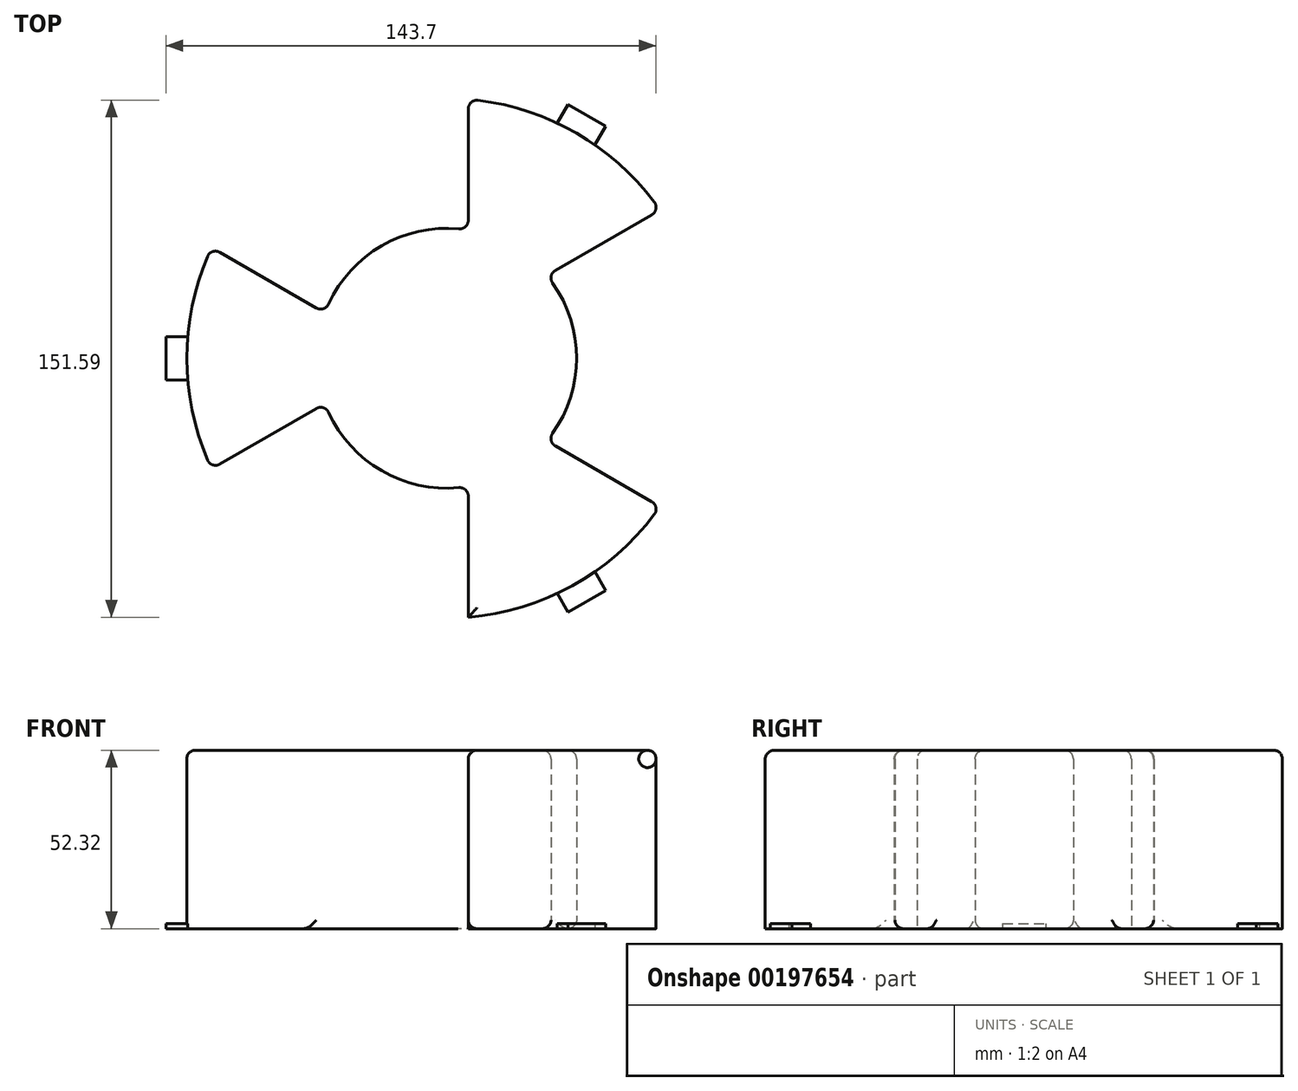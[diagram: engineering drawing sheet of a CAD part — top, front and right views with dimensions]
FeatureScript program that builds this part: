
annotation { "Feature Type Name" : "Feature", "Feature Type Description" : "" }
export const myFeature = defineFeature(function(context is Context, id is Id, definition is map)
    precondition{}
    {
        {
            var Q0;
            Q0=qCreatedBy(makeId("Top.planeOp"),FACE);
            var sketch = newSketch(context, id + "F0", { "sketchPlane" : qUnion([Q0])});
            skCircle(sketch, "E0", {"center": v(0, 0) * mm, "radius": 38.1 * mm});
            skSolve(sketch);
        }
        {
            var Q0;
            Q0 = qSketchRegion(id + "F0", true);
            extrude(context, id + "F1", {"entities" : qUnion([Q0]), "depth" : 52.32 * mm});
        }
        {
            var Q0;
            Q0=qCreatedBy(makeId("Top.planeOp"),FACE);
            var sketch = newSketch(context, id + "F2", { "sketchPlane" : qUnion([Q0])});
            skArc(sketch, "E1", {"start": v(6.35, -75.93) * mm, "mid": v(38.1, -66) * mm, "end": v(62.59, -43.47) * mm});
            skArc(sketch, "E2.0", {"start": v(0, -38.1) * mm, "mid": v(19.05, -33) * mm, "end": v(33, -19.05) * mm});
            skLineSegment(sketch, "E3", {"start": v(33, -19.05) * mm, "end": v(66, -38.1) * mm});
            skLineSegment(sketch, "E4", {"start": v(0, -76.2) * mm, "end": v(0, -38.1) * mm});
            skLineSegment(sketch, "E5.0", {"start": v(6.35, -75.93) * mm, "end": v(6.35, -37.57) * mm});
            skLineSegment(sketch, "E6.0", {"start": v(29.36, -24.28) * mm, "end": v(62.59, -43.47) * mm});
            skArc(sketch, "E7.1.0", {"start": v(33, 19.05) * mm, "mid": v(19.05, 33) * mm, "end": v(0, 38.1) * mm});
            skLineSegment(sketch, "E7.1.1", {"start": v(6.35, 37.57) * mm, "end": v(6.35, 75.93) * mm});
            skArc(sketch, "E7.1.2", {"start": v(62.59, 43.47) * mm, "mid": v(38.1, 66) * mm, "end": v(6.35, 75.93) * mm});
            skLineSegment(sketch, "E7.1.3", {"start": v(62.59, 43.47) * mm, "end": v(29.36, 24.28) * mm});
            skLineSegment(sketch, "E7.1.4", {"start": v(66, 38.1) * mm, "end": v(33, 19.05) * mm});
            skLineSegment(sketch, "E7.1.5", {"start": v(0, 38.1) * mm, "end": v(0, 76.2) * mm});
            skArc(sketch, "E7.2.0", {"start": v(-33, 19.05) * mm, "mid": v(-38.1, 0) * mm, "end": v(-33, -19.05) * mm});
            skLineSegment(sketch, "E7.2.1", {"start": v(-35.7, -13.28) * mm, "end": v(-68.94, -32.47) * mm});
            skArc(sketch, "E7.2.2", {"start": v(-68.94, 32.47) * mm, "mid": v(-76.2, 0) * mm, "end": v(-68.94, -32.47) * mm});
            skLineSegment(sketch, "E7.2.3", {"start": v(-68.94, 32.47) * mm, "end": v(-35.7, 13.28) * mm});
            skLineSegment(sketch, "E7.2.4", {"start": v(-66, 38.1) * mm, "end": v(-33, 19.05) * mm});
            skLineSegment(sketch, "E7.2.5", {"start": v(-33, -19.05) * mm, "end": v(-66, -38.1) * mm});
            skSolve(sketch);
        }
        {
            var Q0;
            Q0 = qSketchRegion(id + "F2", true);
            var Q1;
            Q1=makeQuery(id+"F1.opExtrude","CAP_FACE",FACE,{"disambiguationData":[OSD([sQuery(id+"F0.wireOp",EDGE,"E0")])],"isStart":false});
            extrude(context, id + "F3", {"entities" : qUnion([Q0]), "operationType" : NewBodyOperationType.ADD, "endBound" : BoundingType.UP_TO_SURFACE, "endBoundEntityFace" : qUnion([Q1]), "depth" : 25.4 * mm});
        }
        {
            var Q0;
            Q0=makeQuery(id+"F3.boolean.opBoolean","MERGE",FACE,{"derivedFrom":[makeQuery(id+"F1.opExtrude","CAP_FACE",FACE,{"disambiguationData":[OSD([sQuery(id+"F0.wireOp",EDGE,"E0")])],"isStart":true}),makeQuery(id+"F3.opExtrude","CAP_FACE",FACE,{"disambiguationData":[OSD([sQuery(id+"F2.wireOp",EDGE,"E1"),sQuery(id+"F2.wireOp",EDGE,"E2.0"),sQuery(id+"F2.wireOp",EDGE,"E5.0"),sQuery(id+"F2.wireOp",EDGE,"E6.0")])],"isStart":true}),makeQuery(id+"F3.opExtrude","CAP_FACE",FACE,{"disambiguationData":[OSD([sQuery(id+"F2.wireOp",EDGE,"E7.1.0"),sQuery(id+"F2.wireOp",EDGE,"E7.1.1"),sQuery(id+"F2.wireOp",EDGE,"E7.1.2"),sQuery(id+"F2.wireOp",EDGE,"E7.1.3")])],"isStart":true}),makeQuery(id+"F3.opExtrude","CAP_FACE",FACE,{"disambiguationData":[OSD([sQuery(id+"F2.wireOp",EDGE,"E7.2.0"),sQuery(id+"F2.wireOp",EDGE,"E7.2.1"),sQuery(id+"F2.wireOp",EDGE,"E7.2.2"),sQuery(id+"F2.wireOp",EDGE,"E7.2.3")])],"isStart":true})]});
            var sketch = newSketch(context, id + "F4", { "sketchPlane" : qUnion([Q0])});
            skLineSegment(sketch, "E8.bottom", {"start": v(-75.93, 6.35) * mm, "end": v(-82.28, 6.35) * mm});
            skLineSegment(sketch, "E8.top", {"start": v(-75.93, -6.35) * mm, "end": v(-82.28, -6.35) * mm});
            skLineSegment(sketch, "E8.left", {"start": v(-75.93, 6.35) * mm, "end": v(-75.93, -6.35) * mm});
            skLineSegment(sketch, "E8.right", {"start": v(-82.28, 6.35) * mm, "end": v(-82.28, -6.35) * mm});
            skLineSegment(sketch, "E9.1.0", {"start": v(32.47, -68.94) * mm, "end": v(43.47, -62.59) * mm});
            skLineSegment(sketch, "E9.1.1", {"start": v(43.47, -62.59) * mm, "end": v(46.64, -68.09) * mm});
            skLineSegment(sketch, "E9.1.2", {"start": v(35.64, -74.44) * mm, "end": v(46.64, -68.09) * mm});
            skLineSegment(sketch, "E9.1.3", {"start": v(32.47, -68.94) * mm, "end": v(35.64, -74.44) * mm});
            skLineSegment(sketch, "E9.2.0", {"start": v(43.47, 62.59) * mm, "end": v(32.47, 68.94) * mm});
            skLineSegment(sketch, "E9.2.1", {"start": v(32.47, 68.94) * mm, "end": v(35.64, 74.44) * mm});
            skLineSegment(sketch, "E9.2.2", {"start": v(46.64, 68.09) * mm, "end": v(35.64, 74.44) * mm});
            skLineSegment(sketch, "E9.2.3", {"start": v(43.47, 62.59) * mm, "end": v(46.64, 68.09) * mm});
            skPoint(sketch, "E9.center", {"position": v(0, 0) * mm});
            skSolve(sketch);
        }
        {
            var Q0;
            Q0 = qSketchRegion(id + "F4", true);
            extrude(context, id + "F5", {"entities" : qUnion([Q0]), "operationType" : NewBodyOperationType.ADD, "oppositeDirection" : true, "depth" : 1.52 * mm});
        }
        {
            var Q0;
            {var subQ0=sQuery(id+"F0.wireOp",EDGE,"E0");Q0=makeQuery(id+"F3.boolean.opBoolean","MERGE",FACE,{"derivedFrom":[makeQuery(id+"F1.opExtrude","CAP_FACE",FACE,{"disambiguationData":[OSD([subQ0])],"isStart":false}),makeQuery(id+"F3.opExtrude","CAP_FACE",FACE,{"disambiguationData":[OSD([subQ0]),ownerDisambiguation([makeQuery(id+"F3.opExtrude","SWEPT_BODY",BODY,{"disambiguationData":[OSD([sQuery(id+"F2.wireOp",EDGE,"E1"),sQuery(id+"F2.wireOp",EDGE,"E2.0"),sQuery(id+"F2.wireOp",EDGE,"E5.0"),sQuery(id+"F2.wireOp",EDGE,"E6.0")])]})])],"isStart":false}),makeQuery(id+"F3.opExtrude","CAP_FACE",FACE,{"disambiguationData":[OSD([subQ0]),ownerDisambiguation([makeQuery(id+"F3.opExtrude","SWEPT_BODY",BODY,{"disambiguationData":[OSD([sQuery(id+"F2.wireOp",EDGE,"E7.1.0"),sQuery(id+"F2.wireOp",EDGE,"E7.1.1"),sQuery(id+"F2.wireOp",EDGE,"E7.1.2"),sQuery(id+"F2.wireOp",EDGE,"E7.1.3")])]})])],"isStart":false}),makeQuery(id+"F3.opExtrude","CAP_FACE",FACE,{"disambiguationData":[OSD([subQ0]),ownerDisambiguation([makeQuery(id+"F3.opExtrude","SWEPT_BODY",BODY,{"disambiguationData":[OSD([sQuery(id+"F2.wireOp",EDGE,"E7.2.0"),sQuery(id+"F2.wireOp",EDGE,"E7.2.1"),sQuery(id+"F2.wireOp",EDGE,"E7.2.2"),sQuery(id+"F2.wireOp",EDGE,"E7.2.3")])]})])],"isStart":false})]});}
            var Q1;
            {var subQ0=sQuery(id+"F0.wireOp",EDGE,"E0");var subQ1=sQuery(id+"F2.wireOp",EDGE,"E5.0");Q1=makeQuery(id+"F3.boolean.opBoolean","SPLIT",FACE,{"disambiguationData":[TD([makeQuery(id+"F3.opExtrude","SWEPT_FACE",FACE,{"disambiguationData":[OSD([subQ1])]})])],"derivedFrom":makeQuery(id+"F1.opExtrude","SWEPT_FACE",FACE,{"disambiguationData":[OSD([subQ0])]})});}
            var Q2;
            Q2=makeQuery(id+"F3.opExtrude","SWEPT_EDGE",EDGE,{"disambiguationData":[OSD([sQuery(id+"F2.wireOp",EDGE,"E7.2.1"),sQuery(id+"F2.wireOp",EDGE,"E7.2.2")])]});
            var Q3;
            {var subQ2=sQuery(id+"F2.wireOp",EDGE,"E7.1.1");var subQ8=sQuery(id+"F0.wireOp",EDGE,"E0");Q3=makeQuery(id+"F3.boolean.opBoolean","SPLIT",FACE,{"disambiguationData":[TD([makeQuery(id+"F3.opExtrude","SWEPT_FACE",FACE,{"disambiguationData":[OSD([subQ2])]})])],"derivedFrom":makeQuery(id+"F1.opExtrude","SWEPT_FACE",FACE,{"disambiguationData":[OSD([subQ8])]})});}
            var Q4;
            Q4=makeQuery(id+"F3.opExtrude","SWEPT_EDGE",EDGE,{"disambiguationData":[OSD([sQuery(id+"F2.wireOp",EDGE,"E7.2.2"),sQuery(id+"F2.wireOp",EDGE,"E7.2.3")])]});
            var Q5;
            Q5=makeQuery(id+"F3.opExtrude","SWEPT_EDGE",EDGE,{"disambiguationData":[OSD([sQuery(id+"F2.wireOp",EDGE,"E7.1.1"),sQuery(id+"F2.wireOp",EDGE,"E7.1.2")])]});
            var Q6;
            {var subQ0=sQuery(id+"F2.wireOp",EDGE,"E6.0");var subQ4=sQuery(id+"F0.wireOp",EDGE,"E0");Q6=makeQuery(id+"F3.boolean.opBoolean","SPLIT",FACE,{"disambiguationData":[TD([makeQuery(id+"F3.opExtrude","SWEPT_FACE",FACE,{"disambiguationData":[OSD([subQ0])]})])],"derivedFrom":makeQuery(id+"F1.opExtrude","SWEPT_FACE",FACE,{"disambiguationData":[OSD([subQ4])]})});}
            var Q7;
            Q7=makeQuery(id+"F3.opExtrude","SWEPT_EDGE",EDGE,{"disambiguationData":[OSD([sQuery(id+"F2.wireOp",EDGE,"E7.1.2"),sQuery(id+"F2.wireOp",EDGE,"E7.1.3")])]});
            var Q8;
            Q8=makeQuery(id+"F3.opExtrude","SWEPT_EDGE",EDGE,{"disambiguationData":[OSD([sQuery(id+"F2.wireOp",EDGE,"E1"),sQuery(id+"F2.wireOp",EDGE,"E6.0")])]});
            fillet(context, id + "F6", {"entities" : qUnion([Q0, Q1, Q2, Q3, Q4, Q5, Q6, Q7, Q8]), "radius" : 2.54 * mm, "tangentPropagation" : true, "allowEdgeOverflow" : false});
        }
    });
